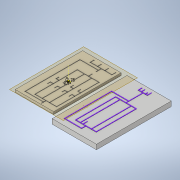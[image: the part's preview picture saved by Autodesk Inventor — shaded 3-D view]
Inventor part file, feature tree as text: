
AUTODESK INVENTOR PART (.ipt)
format: ipt  version: 2021 (Build 250183000, 183)  size: 478,720 bytes
history: native  units: in
note: dims shown in document units (in); Inventor stores cm internally (conversion verified against a paired STEP export)
features: sketch x5, other x4, extrude x4, plane x1, rib x1
ambient origin geometry x8: Origin, YZ Plane, XZ Plane, XY Plane, X Axis, Y Axis, Z Axis, Center Point
bodies: Solid1 (feature_tree)
feature tree (15):
  other  "Board Geometry"
  other  "Valve Geometry"
  other  "Flow Layer channels"
  extrude  "Extrusion1"  Depth=2.7559in
  other  "Channel Geometry"
  extrude  "Extrusion2"  Depth=0.0984in
  sketch  "Sketch7"  dims[d0=1.5748in d2=2.7559in]
  plane  "Work Plane2"
  extrude  "Extrusion3"  Depth=0.0394in
  rib  "Rib7"
  extrude  "Extrusion6"  Depth=0.0197in
  sketch  "Sketch15"  dims[d35=0.0197in d36=0.0197in d37=0.0197in d38=0.0197in d39=0.0197in d40=0.0197in d41=0.0197in d42=0.0197in d43=0.0197in d44=0.0197in d45=0.0197in d47=0.0197in d48=0.0197in d49=0.0197in d50=0.0197in d52=0.0197in d53=0.0197in d54=0.0197in d55=0.0197in d56=0.0197in d57=0.0197in d58=0.0197in d59=0.0197in d60=0.0197in d61=0.0197in d62=0.0197in d63=0.0197in d66=0.0197in d67=0.0197in d68=0.0197in d69=0.0197in d70=0.0197in d71=0.0197in d72=0.0197in d73=0.0197in d74=0.0197in d75=0.0197in d76=0.0197in d77=0.0197in d78=0.0197in d79=0.0197in d80=0.0197in d81=0.0197in d82=0.0197in d83=0.0197in d84=0.0394in d85=0.5906in d86=0.5906in d87=0.5906in d88=0.5906in d89=0.5906in d90=0.5906in d91=0.2362in d92=0.0197in d93=0.1575in d94=1.1811in d96=0.315in d97=2.5591in d98=2.2441in d99=0.315in d100=0.315in d101=0.4724in d102=0.2362in d103=0.2362in d104=0.0394in d105=0.0394in d106=0.0197in d107=0.1575in d108=1.0236in d109=0.1575in d110=0.7874in d111=0.0394in d112=0.0in d120=0.1181in d121=0.0394in d122=0.3937in d123=0.0in d164=0.0394in d165=0.0394in d166=0.0in d167=0.0in d168=0.0394in d169=0.0394in d172=0.0787in d173=0.0in d174=0.0197in d175=0.0344in]
  sketch  "Sketch8"  dims[d4=0.0689in d5=0.0984in]
  sketch  "Sketch9"  dims[d17=0.1969in d18=0.0in d19=0.0394in]
  sketch  "Sketch14"  dims[d21=0.0394in d34=0.0197in]
